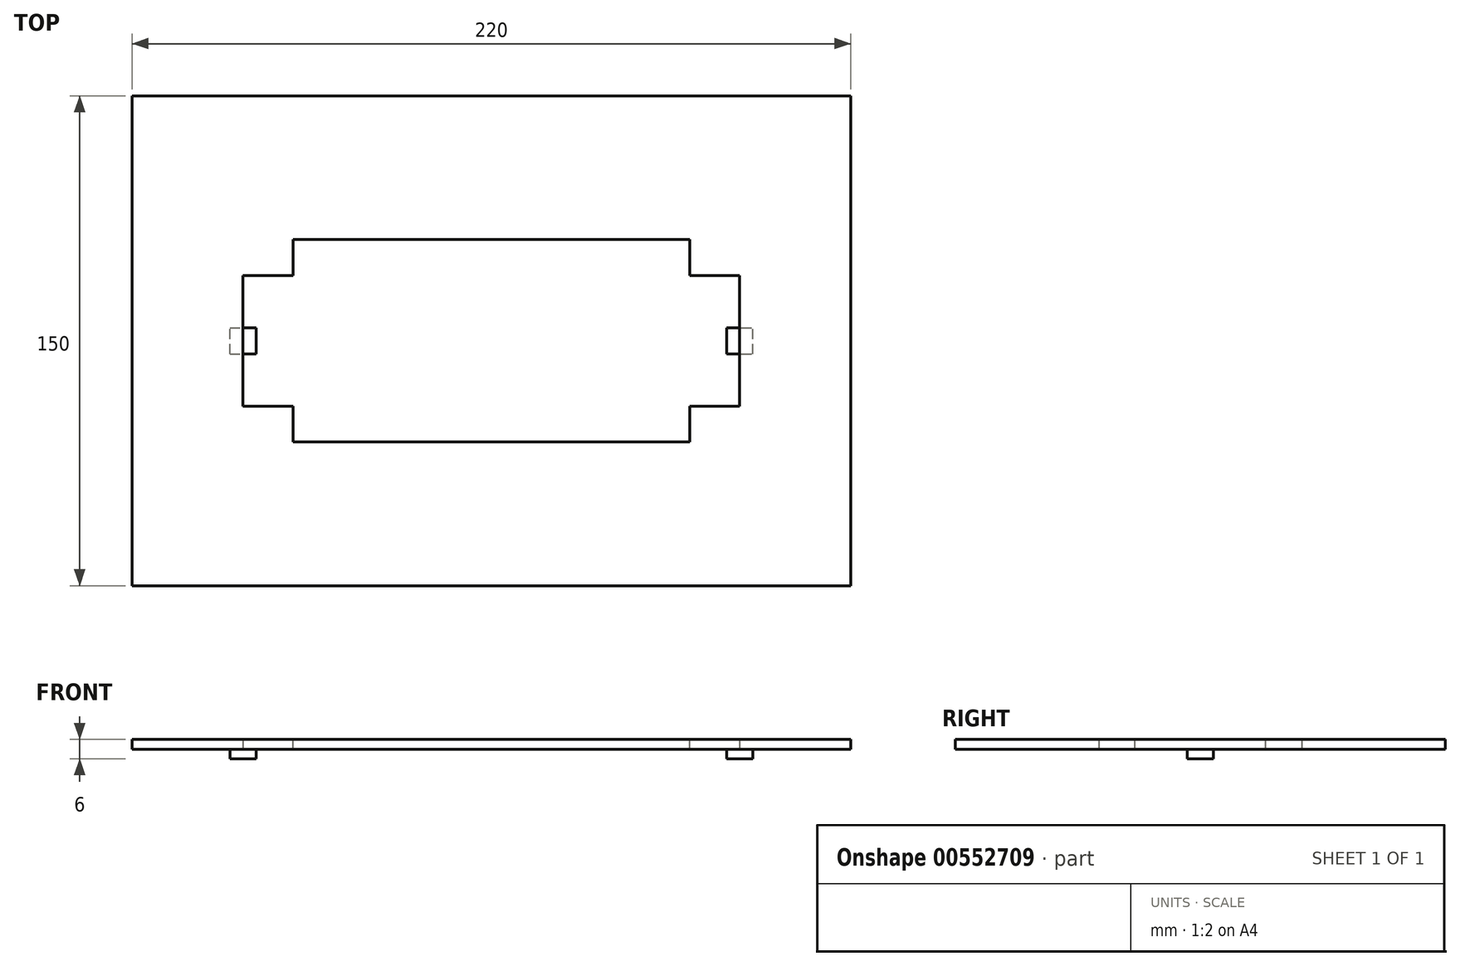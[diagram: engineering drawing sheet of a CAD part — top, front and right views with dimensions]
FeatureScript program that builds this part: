
annotation { "Feature Type Name" : "Feature", "Feature Type Description" : "" }
export const myFeature = defineFeature(function(context is Context, id is Id, definition is map)
    precondition{}
    {
        {
            var Q0;
            Q0=qCreatedBy(makeId("Top.planeOp"),FACE);
            var sketch = newSketch(context, id + "F0", { "sketchPlane" : qUnion([Q0])});
            skLineSegment(sketch, "E0.bottom", {"start": v(0, 0) * mm, "end": v(220, 0) * mm});
            skLineSegment(sketch, "E0.top", {"start": v(0, -150) * mm, "end": v(220, -150) * mm});
            skLineSegment(sketch, "E0.left", {"start": v(0, 0) * mm, "end": v(0, -150) * mm});
            skLineSegment(sketch, "E0.right", {"start": v(220, 0) * mm, "end": v(220, -150) * mm});
            skSolve(sketch);
        }
        {
            var Q0;
            Q0=makeQuery(id+"F0.imprint","IMPRINT",FACE,{"disambiguationData":[TD([[makeQuery(id+"F0.imprint","IMPRINT",EDGE,{"derivedFrom":sQuery(id+"F0.wireOp",EDGE,"E0.bottom")}),-1.0]])]});
            var sketch = newSketch(context, id + "F1", { "sketchPlane" : qUnion([Q0])});
            skLineSegment(sketch, "E1.bottom", {"start": v(34, -55) * mm, "end": v(186, -55) * mm});
            skLineSegment(sketch, "E1.top", {"start": v(34, -95) * mm, "end": v(186, -95) * mm});
            skLineSegment(sketch, "E1.left", {"start": v(34, -55) * mm, "end": v(34, -95) * mm});
            skLineSegment(sketch, "E1.right", {"start": v(186, -55) * mm, "end": v(186, -95) * mm});
            skSolve(sketch);
        }
        {
            var Q0;
            Q0=makeQuery(id+"F0.imprint","IMPRINT",FACE,{"disambiguationData":[TD([[makeQuery(id+"F0.imprint","IMPRINT",EDGE,{"derivedFrom":sQuery(id+"F0.wireOp",EDGE,"E0.bottom")}),-1.0]])]});
            var sketch = newSketch(context, id + "F2", { "sketchPlane" : qUnion([Q0])});
            skLineSegment(sketch, "E2.bottom", {"start": v(49.25, -44) * mm, "end": v(170.75, -44) * mm});
            skLineSegment(sketch, "E2.top", {"start": v(49.25, -106) * mm, "end": v(170.75, -106) * mm});
            skLineSegment(sketch, "E2.left", {"start": v(49.25, -44) * mm, "end": v(49.25, -106) * mm});
            skLineSegment(sketch, "E2.right", {"start": v(170.75, -44) * mm, "end": v(170.75, -106) * mm});
            skSolve(sketch);
        }
        {
            var Q0;
            Q0=makeQuery(id+"F2.imprint","IMPRINT",FACE,{"disambiguationData":[TD([[makeQuery(id+"F2.imprint","IMPRINT",EDGE,{"derivedFrom":sQuery(id+"F2.wireOp",EDGE,"E2.bottom")}),1.0]])]});
            extrude(context, id + "F3", {"entities" : qUnion([Q0]), "depth" : 3 * mm, "offsetDistance" : 25 * mm});
        }
        {
            var Q0;
            Q0=makeQuery(id+"F1.imprint","IMPRINT",FACE,{"disambiguationData":[TD([[makeQuery(id+"F1.imprint","IMPRINT",EDGE,{"derivedFrom":sQuery(id+"F1.wireOp",EDGE,"E1.bottom")}),-1.0]])]});
            extrude(context, id + "F4", {"entities" : qUnion([Q0]), "operationType" : NewBodyOperationType.REMOVE, "depth" : 3 * mm, "offsetDistance" : 25 * mm});
        }
        {
            var Q0;
            Q0=makeQuery(id+"F0.imprint","IMPRINT",FACE,{"disambiguationData":[TD([[makeQuery(id+"F0.imprint","IMPRINT",EDGE,{"derivedFrom":sQuery(id+"F0.wireOp",EDGE,"E0.bottom")}),-1.0]])]});
            var sketch = newSketch(context, id + "F5", { "sketchPlane" : qUnion([Q0])});
            skLineSegment(sketch, "E3.bottom", {"start": v(30, -79) * mm, "end": v(38, -79) * mm});
            skLineSegment(sketch, "E3.top", {"start": v(30, -71) * mm, "end": v(38, -71) * mm});
            skLineSegment(sketch, "E3.left", {"start": v(30, -79) * mm, "end": v(30, -71) * mm});
            skLineSegment(sketch, "E3.right", {"start": v(38, -79) * mm, "end": v(38, -71) * mm});
            skSolve(sketch);
        }
        {
            var Q0;
            Q0=makeQuery(id+"F0.imprint","IMPRINT",FACE,{"disambiguationData":[TD([[makeQuery(id+"F0.imprint","IMPRINT",EDGE,{"derivedFrom":sQuery(id+"F0.wireOp",EDGE,"E0.bottom")}),-1.0]])]});
            var sketch = newSketch(context, id + "F6", { "sketchPlane" : qUnion([Q0])});
            skLineSegment(sketch, "E4.bottom", {"start": v(182, -79) * mm, "end": v(190, -79) * mm});
            skLineSegment(sketch, "E4.top", {"start": v(182, -71) * mm, "end": v(190, -71) * mm});
            skLineSegment(sketch, "E4.left", {"start": v(182, -79) * mm, "end": v(182, -71) * mm});
            skLineSegment(sketch, "E4.right", {"start": v(190, -79) * mm, "end": v(190, -71) * mm});
            skSolve(sketch);
        }
        {
            var Q0;
            Q0 = qSketchRegion(id + "F5", true);
            extrude(context, id + "F7", {"entities" : qUnion([Q0]), "operationType" : NewBodyOperationType.ADD, "oppositeDirection" : true, "depth" : 3 * mm, "offsetDistance" : 25 * mm});
        }
        {
            var Q0;
            Q0=makeQuery(id+"F6.imprint","IMPRINT",FACE,{"disambiguationData":[TD([[makeQuery(id+"F6.imprint","IMPRINT",EDGE,{"derivedFrom":sQuery(id+"F6.wireOp",EDGE,"E4.bottom")}),1.0]])]});
            extrude(context, id + "F8", {"entities" : qUnion([Q0]), "operationType" : NewBodyOperationType.ADD, "oppositeDirection" : true, "depth" : 3 * mm, "offsetDistance" : 25 * mm});
        }
    });
